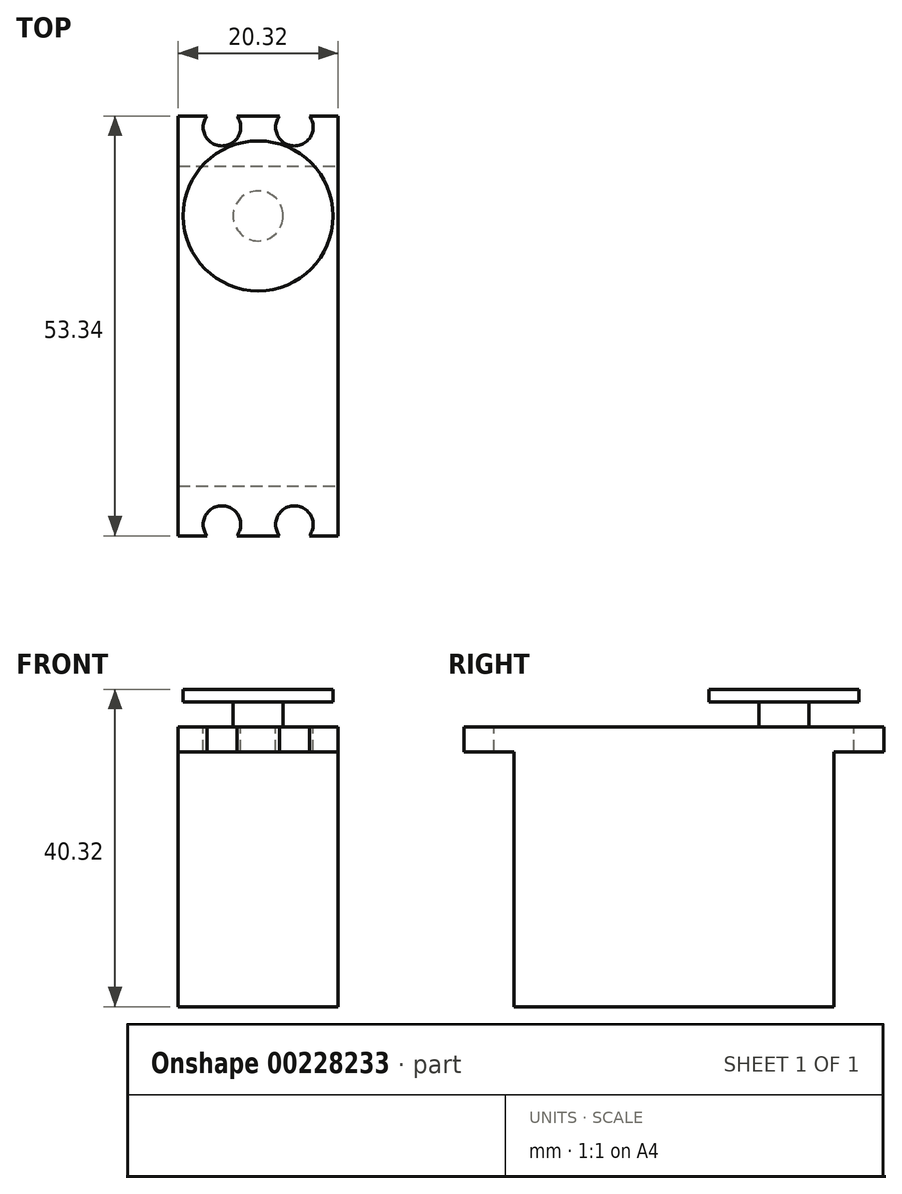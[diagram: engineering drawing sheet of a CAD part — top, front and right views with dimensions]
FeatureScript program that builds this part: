
annotation { "Feature Type Name" : "Feature", "Feature Type Description" : "" }
export const myFeature = defineFeature(function(context is Context, id is Id, definition is map)
    precondition{}
    {
        {
            var Q0;
            Q0=qCreatedBy(makeId("Top.planeOp"),FACE);
            var sketch = newSketch(context, id + "F0", { "sketchPlane" : qUnion([Q0])});
            skLineSegment(sketch, "E0.bottom", {"start": v(-10.16, 20.32) * mm, "end": v(10.16, 20.32) * mm});
            skLineSegment(sketch, "E0.top", {"start": v(-10.16, -20.32) * mm, "end": v(10.16, -20.32) * mm});
            skLineSegment(sketch, "E0.left", {"start": v(-10.16, 20.32) * mm, "end": v(-10.16, -20.32) * mm});
            skLineSegment(sketch, "E0.right", {"start": v(10.16, 20.32) * mm, "end": v(10.16, -20.32) * mm});
            skPoint(sketch, "E0.middle", {"position": v(0, 0) * mm});
            skSolve(sketch);
        }
        {
            var Q0;
            Q0 = qSketchRegion(id + "F0", true);
            extrude(context, id + "F1", {"entities" : qUnion([Q0]), "depth" : 35.56 * mm});
        }
        {
            var Q0;
            Q0=makeQuery(id+"F1.opExtrude","CAP_FACE",FACE,{"disambiguationData":[OSD([sQuery(id+"F0.wireOp",EDGE,"E0.bottom"),sQuery(id+"F0.wireOp",EDGE,"E0.top"),sQuery(id+"F0.wireOp",EDGE,"E0.left"),sQuery(id+"F0.wireOp",EDGE,"E0.right")])],"isStart":false});
            var sketch = newSketch(context, id + "F2", { "sketchPlane" : qUnion([Q0])});
            skLineSegment(sketch, "E1.bottom", {"start": v(-10.16, 20.32) * mm, "end": v(10.16, 20.32) * mm});
            skLineSegment(sketch, "E1.top", {"start": v(-10.16, 26.67) * mm, "end": v(10.16, 26.67) * mm});
            skLineSegment(sketch, "E1.left", {"start": v(-10.16, 20.32) * mm, "end": v(-10.16, 26.67) * mm});
            skLineSegment(sketch, "E1.right", {"start": v(10.16, 20.32) * mm, "end": v(10.16, 26.67) * mm});
            skCircle(sketch, "E2", {"center": v(-4.6, 25.24) * mm, "radius": 2.38 * mm});
            skPoint(sketch, "E2.centerSnap0", {"position": v(-10.16, 25.24) * mm});
            skCircle(sketch, "E3.MirrorC", {"center": v(4.6, 25.24) * mm, "radius": 2.38 * mm});
            skLineSegment(sketch, "E4.MirrorCS", {"start": v(10.16, -20.32) * mm, "end": v(10.16, -26.67) * mm});
            skLineSegment(sketch, "E5.MirrorCS", {"start": v(-10.16, -26.67) * mm, "end": v(10.16, -26.67) * mm});
            skCircle(sketch, "E6.MirrorC", {"center": v(4.6, -25.24) * mm, "radius": 2.38 * mm});
            skCircle(sketch, "E7.MirrorC", {"center": v(-4.6, -25.24) * mm, "radius": 2.38 * mm});
            skLineSegment(sketch, "E8.MirrorCS", {"start": v(-10.16, -20.32) * mm, "end": v(-10.16, -26.67) * mm});
            skSolve(sketch);
        }
        {
            var Q0;
            Q0=makeQuery(id+"F2.imprint","IMPRINT",FACE,{"disambiguationData":[TD([[makeQuery(id+"F2.imprint","IMPRINT",EDGE,{"derivedFrom":sQuery(id+"F2.wireOp",EDGE,"E1.bottom")}),1.0]])]});
            var Q1;
            {var subQ1=sQuery(id+"F2.wireOp",EDGE,"E4.MirrorCS");Q1=makeQuery(id+"F2.imprint","IMPRINT",FACE,{"disambiguationData":[TD([[makeQuery(id+"F2.imprint","IMPRINT",EDGE,{"derivedFrom":subQ1}),-1.0]])]});}
            extrude(context, id + "F3", {"entities" : qUnion([Q0, Q1]), "operationType" : NewBodyOperationType.ADD, "oppositeDirection" : true, "depth" : 3.17 * mm});
        }
        {
            var Q0;
            Q0=makeQuery(id+"F1.opExtrude","CAP_FACE",FACE,{"disambiguationData":[OSD([sQuery(id+"F0.wireOp",EDGE,"E0.bottom"),sQuery(id+"F0.wireOp",EDGE,"E0.top"),sQuery(id+"F0.wireOp",EDGE,"E0.left"),sQuery(id+"F0.wireOp",EDGE,"E0.right")])],"isStart":false});
            var sketch = newSketch(context, id + "F4", { "sketchPlane" : qUnion([Q0])});
            skCircle(sketch, "E9", {"center": v(0, 13.97) * mm, "radius": 3.18 * mm});
            skPoint(sketch, "E9.centerSnap0", {"position": v(0, 20.32) * mm});
            skSolve(sketch);
        }
        {
            var Q0;
            Q0 = qSketchRegion(id + "F4", true);
            extrude(context, id + "F5", {"entities" : qUnion([Q0]), "operationType" : NewBodyOperationType.ADD, "depth" : 3.17 * mm});
        }
        {
            var Q0;
            Q0=makeQuery(id+"F5.opExtrude","CAP_FACE",FACE,{"disambiguationData":[OSD([sQuery(id+"F4.wireOp",EDGE,"E9")])],"isStart":false});
            var sketch = newSketch(context, id + "F6", { "sketchPlane" : qUnion([Q0])});
            skCircle(sketch, "E10", {"center": v(0, 13.97) * mm, "radius": 9.53 * mm});
            skSolve(sketch);
        }
        {
            var Q0;
            Q0 = qSketchRegion(id + "F6", true);
            extrude(context, id + "F7", {"entities" : qUnion([Q0]), "operationType" : NewBodyOperationType.ADD, "depth" : 1.59 * mm});
        }
    });
